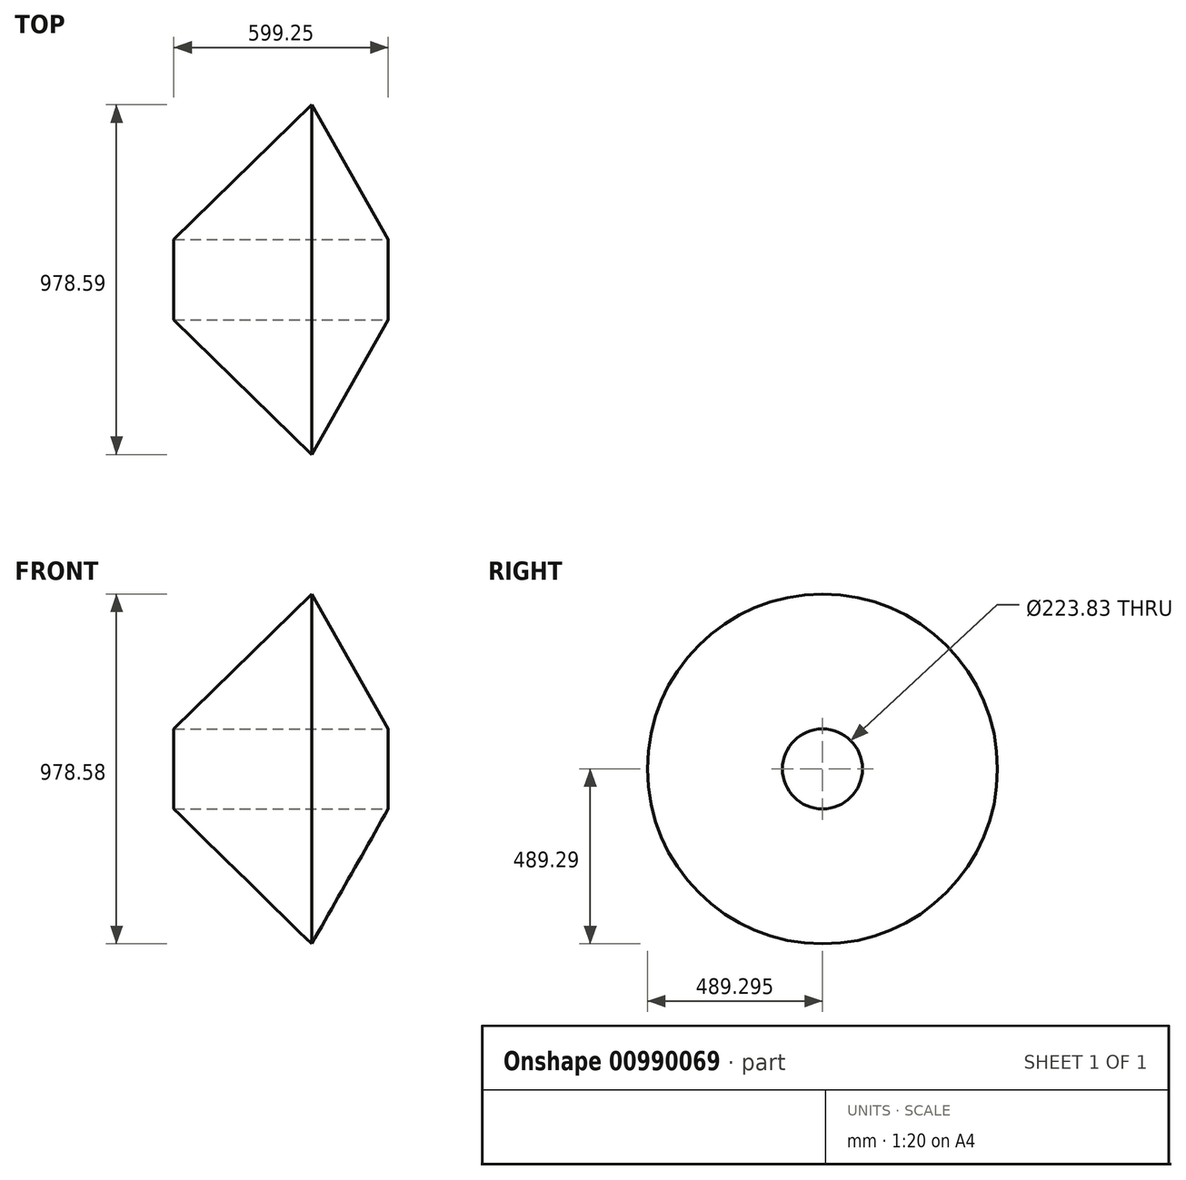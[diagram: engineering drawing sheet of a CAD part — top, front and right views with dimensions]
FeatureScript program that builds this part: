
annotation { "Feature Type Name" : "Feature", "Feature Type Description" : "" }
export const myFeature = defineFeature(function(context is Context, id is Id, definition is map)
    precondition{}
    {
        {
            var Q0;
            Q0=qCreatedBy(makeId("Top.planeOp"),FACE);
            var sketch = newSketch(context, id + "F0", { "sketchPlane" : qUnion([Q0])});
            skLineSegment(sketch, "E0", {"start": v(0, -377.38) * mm, "end": v(-385.13, 0) * mm});
            skLineSegment(sketch, "E1", {"start": v(-385.13, 0) * mm, "end": v(214.12, 0) * mm});
            skLineSegment(sketch, "E2", {"start": v(214.12, 0) * mm, "end": v(0, -377.38) * mm});
            skSolve(sketch);
        }
        {
            var Q0;
            Q0=qCreatedBy(makeId("Top.planeOp"),FACE);
            var sketch = newSketch(context, id + "F1", { "sketchPlane" : qUnion([Q0])});
            skLineSegment(sketch, "E3", {"start": v(200.14, 111.92) * mm, "end": v(-411.28, 111.92) * mm});
            skSolve(sketch);
        }
        {
            var Q0;
            Q0=makeQuery(id+"F0.imprint","IMPRINT",FACE,{"disambiguationData":[TD([[makeQuery(id+"F0.imprint","IMPRINT",EDGE,{"derivedFrom":sQuery(id+"F0.wireOp",EDGE,"E0")}),-1.0]])]});
            var Q1;
            Q1=sQuery(id+"F1.wireOp",EDGE,"E3");
            revolve(context, id + "F2", {"surfaceOperationType" : NewSurfaceOperationType.NEW, "entities" : qUnion([Q0]), "axis" : qUnion([Q1]), "revolveType" : RevolveType.FULL});
        }
    });
